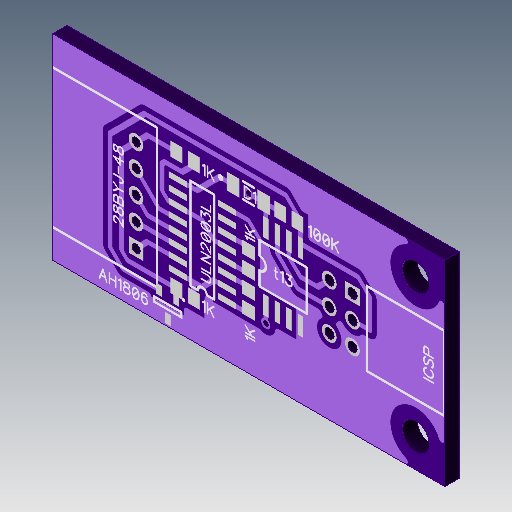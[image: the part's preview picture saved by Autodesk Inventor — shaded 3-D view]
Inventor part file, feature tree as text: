
AUTODESK INVENTOR PART (.ipt)
format: ipt  version: 2018 (Build 220112000, 112)  size: 284,672 bytes
history: native  units: mm
features: other x4, sketch x2
ambient origin geometry x8: Origin, YZ Plane, XZ Plane, XY Plane, X Axis, Y Axis, Z Axis, Center Point
bodies: Solid1 (feature_tree)
feature tree (6):
  other  "Decal1"
  other  "Decal2"
  sketch  "Sketch1"
  other  "Image1"
  sketch  "Sketch2"
  other  "Image2"
